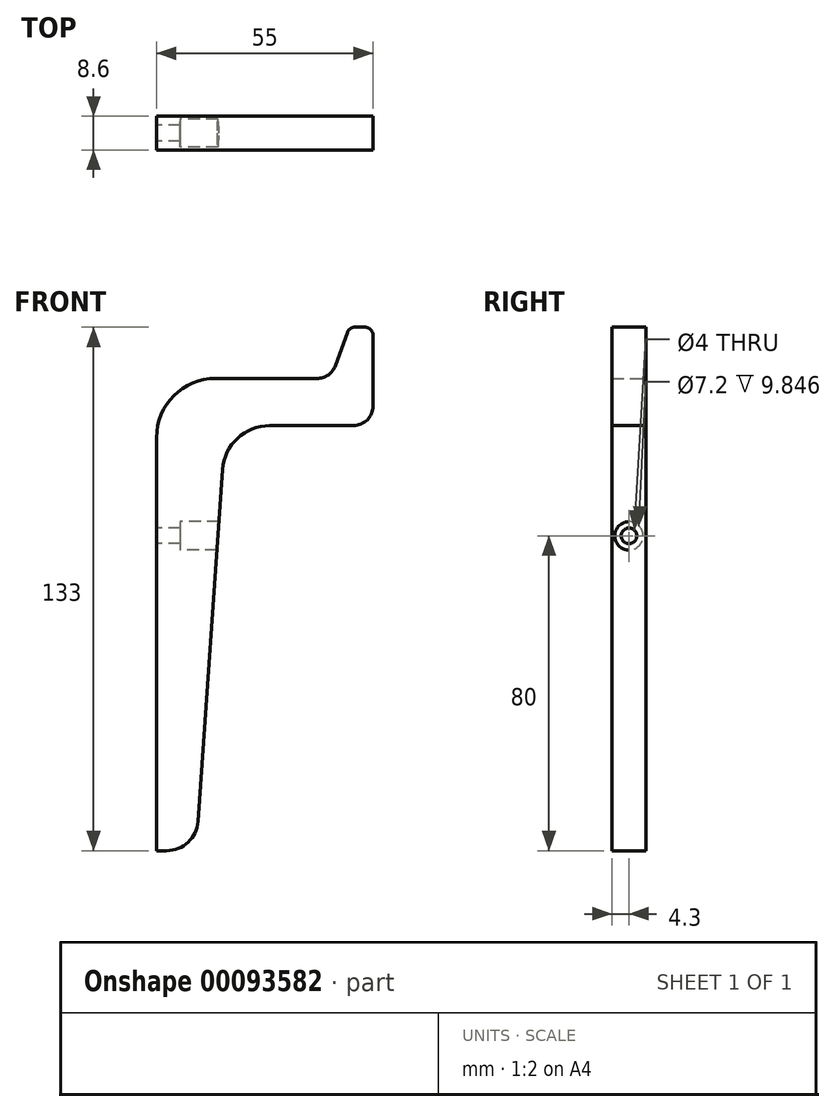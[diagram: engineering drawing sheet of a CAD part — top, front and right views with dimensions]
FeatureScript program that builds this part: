
annotation { "Feature Type Name" : "Feature", "Feature Type Description" : "" }
export const myFeature = defineFeature(function(context is Context, id is Id, definition is map)
    precondition{}
    {
        {
            var Q0;
            Q0=qCreatedBy(makeId("Front.planeOp"),FACE);
            var sketch = newSketch(context, id + "F0", { "sketchPlane" : qUnion([Q0])});
            skLineSegment(sketch, "E0", {"start": v(0, 0) * mm, "end": v(0, 120) * mm});
            skLineSegment(sketch, "E1", {"start": v(0, 0) * mm, "end": v(10, 0) * mm});
            skLineSegment(sketch, "E2", {"start": v(10, 0) * mm, "end": v(17.55, 108) * mm});
            skLineSegment(sketch, "E3", {"start": v(17.55, 108) * mm, "end": v(55, 108) * mm});
            skLineSegment(sketch, "E4", {"start": v(55, 108) * mm, "end": v(55, 133) * mm});
            skLineSegment(sketch, "E5", {"start": v(55, 133) * mm, "end": v(49, 133) * mm});
            skLineSegment(sketch, "E6", {"start": v(49, 133) * mm, "end": v(44.27, 120) * mm});
            skLineSegment(sketch, "E7", {"start": v(44.27, 120) * mm, "end": v(0, 120) * mm});
            skSolve(sketch);
        }
        {
            var Q0;
            Q0 = qSketchRegion(id + "F0", true);
            extrude(context, id + "F1", {"entities" : qUnion([Q0]), "depth" : 8.6 * mm});
        }
        {
            var Q0;
            Q0=makeQuery(id+"F1.opExtrude","SWEPT_EDGE",EDGE,{"disambiguationData":[OSD([sQuery(id+"F0.wireOp",EDGE,"E2"),sQuery(id+"F0.wireOp",EDGE,"E3")])]});
            fillet(context, id + "F2", {"entities" : qUnion([Q0]), "radius" : 12 * mm, "tangentPropagation" : true, "allowEdgeOverflow" : false});
        }
        {
            var Q0;
            Q0=makeQuery(id+"F1.opExtrude","SWEPT_EDGE",EDGE,{"disambiguationData":[OSD([sQuery(id+"F0.wireOp",EDGE,"E1"),sQuery(id+"F0.wireOp",EDGE,"E2")])]});
            fillet(context, id + "F3", {"entities" : qUnion([Q0]), "radius" : 8 * mm, "tangentPropagation" : true, "allowEdgeOverflow" : false});
        }
        {
            var Q0;
            Q0=makeQuery(id+"F1.opExtrude","SWEPT_EDGE",EDGE,{"disambiguationData":[OSD([sQuery(id+"F0.wireOp",EDGE,"E0"),sQuery(id+"F0.wireOp",EDGE,"E7")])]});
            fillet(context, id + "F4", {"entities" : qUnion([Q0]), "radius" : 15 * mm, "tangentPropagation" : true, "allowEdgeOverflow" : false});
        }
        {
            var Q0;
            Q0=makeQuery(id+"F1.opExtrude","SWEPT_EDGE",EDGE,{"disambiguationData":[OSD([sQuery(id+"F0.wireOp",EDGE,"E3"),sQuery(id+"F0.wireOp",EDGE,"E4")])]});
            fillet(context, id + "F5", {"entities" : qUnion([Q0]), "radius" : 5 * mm, "tangentPropagation" : true, "allowEdgeOverflow" : false});
        }
        {
            var Q0;
            Q0=makeQuery(id+"F1.opExtrude","SWEPT_EDGE",EDGE,{"disambiguationData":[OSD([sQuery(id+"F0.wireOp",EDGE,"E6"),sQuery(id+"F0.wireOp",EDGE,"E7")])]});
            fillet(context, id + "F6", {"entities" : qUnion([Q0]), "radius" : 5 * mm, "tangentPropagation" : true, "allowEdgeOverflow" : false});
        }
        {
            var Q0;
            Q0=makeQuery(id+"F1.opExtrude","SWEPT_EDGE",EDGE,{"disambiguationData":[OSD([sQuery(id+"F0.wireOp",EDGE,"E5"),sQuery(id+"F0.wireOp",EDGE,"E6")])]});
            var Q1;
            Q1=makeQuery(id+"F1.opExtrude","SWEPT_EDGE",EDGE,{"disambiguationData":[OSD([sQuery(id+"F0.wireOp",EDGE,"E4"),sQuery(id+"F0.wireOp",EDGE,"E5")])]});
            fillet(context, id + "F7", {"entities" : qUnion([Q0, Q1]), "radius" : 2 * mm, "tangentPropagation" : true, "allowEdgeOverflow" : false});
        }
        {
            var Q0;
            Q0=makeQuery(id+"F1.opExtrude","SWEPT_FACE",FACE,{"disambiguationData":[OSD([sQuery(id+"F0.wireOp",EDGE,"E0")])]});
            var sketch = newSketch(context, id + "F8", { "sketchPlane" : qUnion([Q0])});
            skLineSegment(sketch, "E8", {"start": v(4.3, 0) * mm, "end": v(4.3, 80) * mm, "construction": true});
            skCircle(sketch, "E9", {"center": v(4.3, 80) * mm, "radius": 2 * mm});
            skSolve(sketch);
        }
        {
            var Q0;
            Q0 = qSketchRegion(id + "F8", true);
            extrude(context, id + "F9", {"entities" : qUnion([Q0]), "operationType" : NewBodyOperationType.REMOVE, "oppositeDirection" : true, "depth" : 25 * mm});
        }
        {
            var Q0;
            Q0=makeQuery(id+"F1.opExtrude","SWEPT_FACE",FACE,{"disambiguationData":[OSD([sQuery(id+"F0.wireOp",EDGE,"E0")])]});
            var sketch = newSketch(context, id + "F10", { "sketchPlane" : qUnion([Q0])});
            skCircle(sketch, "E10", {"center": v(4.3, 80) * mm, "radius": 3.6 * mm});
            skSolve(sketch);
        }
        {
            var Q0;
            Q0 = qSketchRegion(id + "F10", true);
            extrude(context, id + "F11", {"entities" : qUnion([Q0]), "operationType" : NewBodyOperationType.REMOVE, "oppositeDirection" : true, "depth" : 25 * mm, "hasSecondDirection" : true, "secondDirectionOppositeDirection" : true, "secondDirectionDepth" : 6 * mm});
        }
    });
